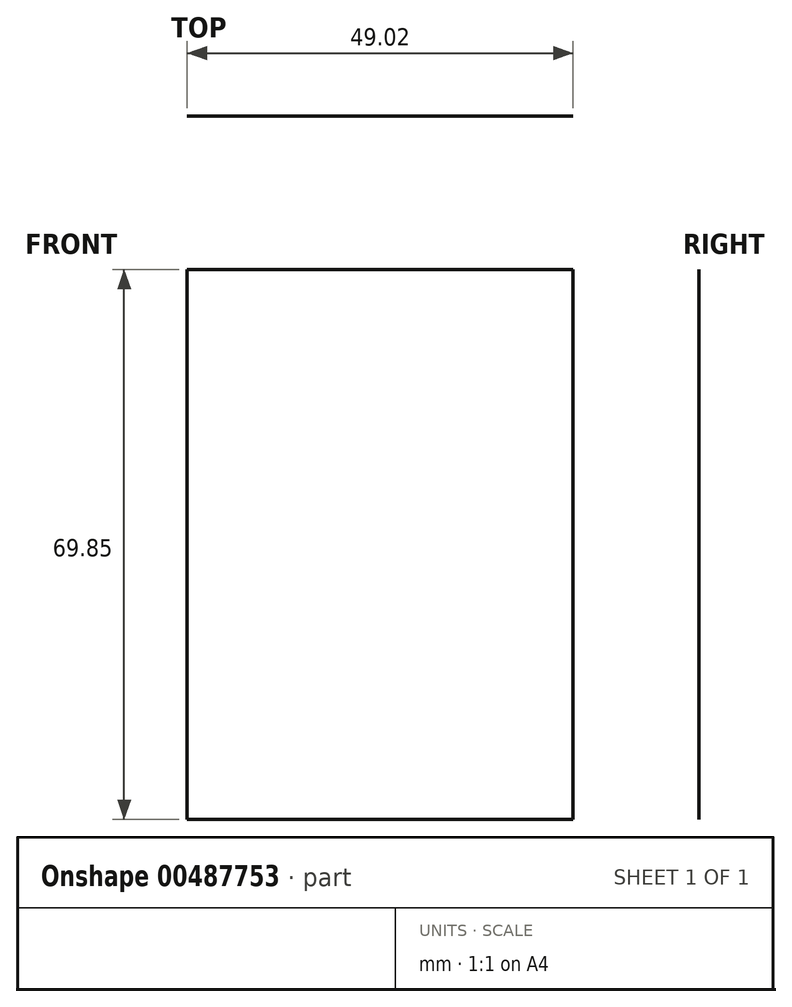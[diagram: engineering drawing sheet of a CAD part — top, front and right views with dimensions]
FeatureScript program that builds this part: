
annotation { "Feature Type Name" : "Feature", "Feature Type Description" : "" }
export const myFeature = defineFeature(function(context is Context, id is Id, definition is map)
    precondition{}
    {
        {
            var Q0;
            Q0=qCreatedBy(makeId("Front.planeOp"),FACE);
            var sketch = newSketch(context, id + "F0", { "sketchPlane" : qUnion([Q0])});
            skLineSegment(sketch, "E0.bottom", {"start": v(0, 0) * mm, "end": v(49.02, 0) * mm});
            skLineSegment(sketch, "E0.top", {"start": v(0, 69.85) * mm, "end": v(49.02, 69.85) * mm});
            skLineSegment(sketch, "E0.left", {"start": v(0, 0) * mm, "end": v(0, 69.85) * mm});
            skLineSegment(sketch, "E0.right", {"start": v(49.02, 0) * mm, "end": v(49.02, 69.85) * mm});
            skSolve(sketch);
        }
        {
            var Q0;
            Q0 = qSketchRegion(id + "F0", true);
            extrude(context, id + "F1", {"entities" : qUnion([Q0]), "depth" : 1 / 203.2 * mm});
        }
    });
